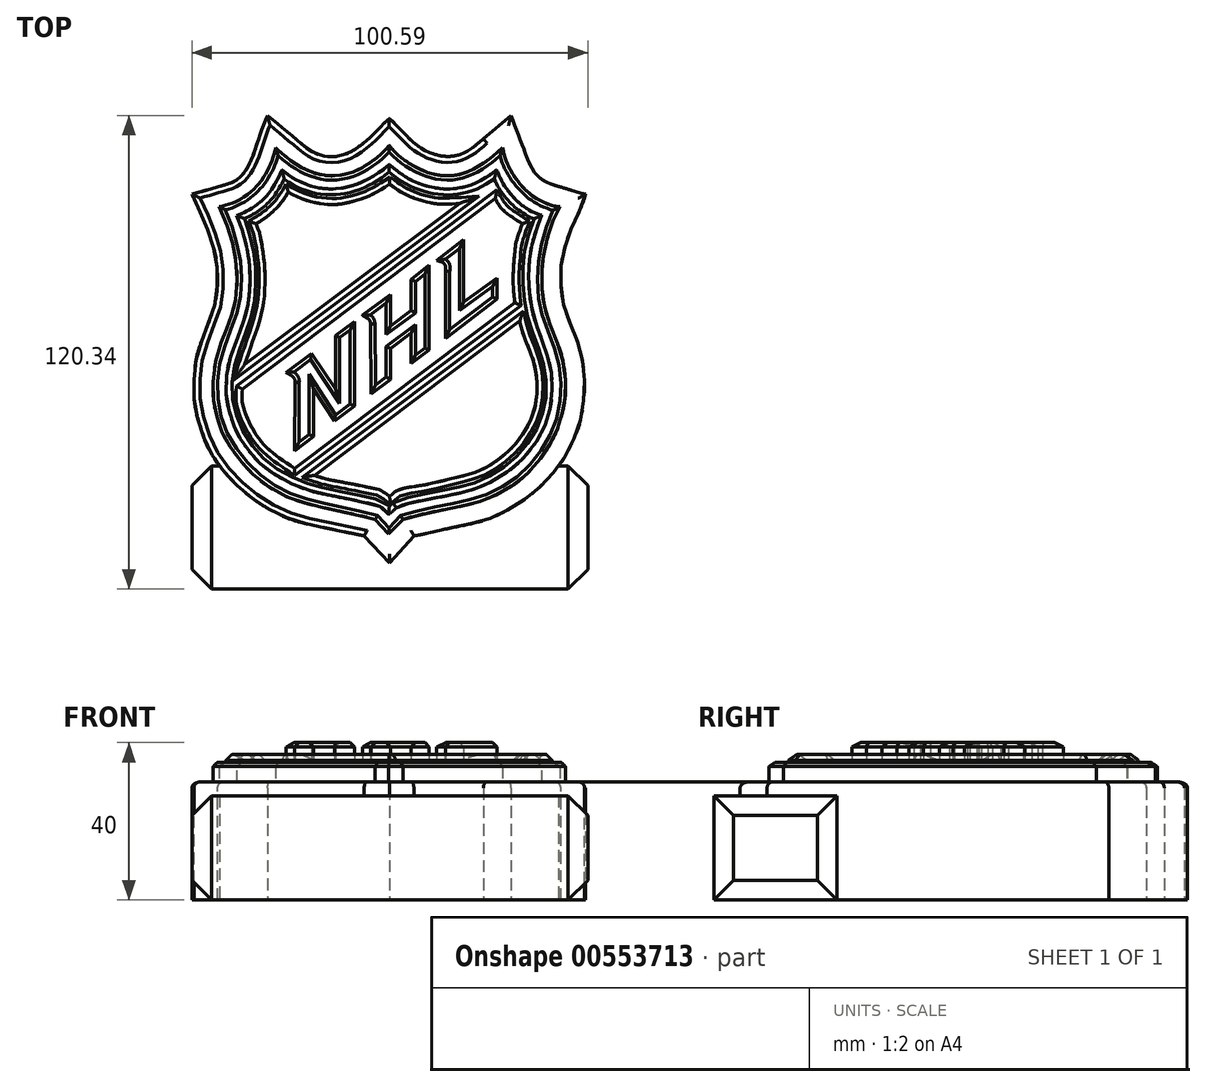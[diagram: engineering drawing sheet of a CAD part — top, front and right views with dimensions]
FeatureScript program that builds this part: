
annotation { "Feature Type Name" : "Feature", "Feature Type Description" : "" }
export const myFeature = defineFeature(function(context is Context, id is Id, definition is map)
    precondition{}
    {
        {
            var Q0;
            Q0=qCreatedBy(makeId("Top.planeOp"),FACE);
            var sketch = newSketch(context, id + "F0", { "sketchPlane" : qUnion([Q0])});
            skLineSegment(sketch, "E0", {"start": v(50, 113.85) * mm, "end": v(50, 0) * mm, "construction": true});
            skLineSegment(sketch, "E1", {"start": v(0, 56.93) * mm, "end": v(100, 56.93) * mm, "construction": true});
            skFitSpline(sketch, "E2", {"points": [v(19.23, 113.85) * mm, v(27.56, 106.9) * mm, v(30.56, 104.67) * mm, v(33.56, 103.56) * mm, v(37.49, 103.58) * mm, v(41.05, 105.05) * mm, v(45.06, 108.09) * mm, v(48.5, 111.55) * mm, v(50.17, 113.1) * mm], "startDerivative": vector(48.33, -40.51) * mm, "endDerivative": vector(17.24, 15.33) * mm});
            skFitSpline(sketch, "E3", {"points": [v(50.17, 113.1) * mm, v(52.88, 110.37) * mm, v(56.85, 106.54) * mm, v(59.8, 104.69) * mm, v(64.07, 103.49) * mm, v(69, 104.28) * mm, v(74.05, 107.95) * mm], "startDerivative": vector(16.76, -16.86) * mm, "endDerivative": vector(25.56, 22.35) * mm});
            skFitSpline(sketch, "E4", {"points": [v(74.05, 107.95) * mm, v(81.12, 113.81) * mm], "startDerivative": vector(7.07, 5.86) * mm, "endDerivative": vector(7.07, 5.86) * mm});
            skFitSpline(sketch, "E5", {"points": [v(81.12, 113.81) * mm, v(81.69, 112.23) * mm, v(82.46, 110.17) * mm, v(83.47, 107.49) * mm, v(84.8, 103.88) * mm, v(85.65, 101.74) * mm, v(87.45, 98.94) * mm, v(89.7, 97.08) * mm, v(92.96, 95.88) * mm, v(97.7, 94.47) * mm, v(100, 93.85) * mm], "startDerivative": vector(7.22, -20.27) * mm, "endDerivative": vector(22.72, -5.9) * mm});
            skFitSpline(sketch, "E6", {"points": [v(100, 93.85) * mm, v(99.63, 92.56) * mm, v(98.68, 90.12) * mm, v(97.69, 87.95) * mm, v(96.72, 85.83) * mm, v(95.29, 82.28) * mm, v(94.02, 77.13) * mm, v(93.73, 74.43) * mm, v(93.84, 69.89) * mm, v(94.57, 65.37) * mm, v(96.14, 60.78) * mm, v(97.7, 56.93) * mm, v(98.46, 54.7) * mm, v(99.33, 50.7) * mm, v(99.66, 47.48) * mm, v(99.7, 44.06) * mm, v(99.26, 39.32) * mm, v(98.41, 35.15) * mm, v(96.8, 31.22) * mm, v(94.63, 26.9) * mm, v(91.9, 23.25) * mm, v(87.6, 18.78) * mm, v(82.5, 15.03) * mm, v(77.28, 12.13) * mm, v(72.01, 10.37) * mm, v(65.55, 9) * mm, v(59.09, 7.54) * mm, v(56.38, 7.05) * mm], "startDerivative": vector(-14.58, -55.75) * mm, "endDerivative": vector(-79.32, -12.44) * mm});
            skFitSpline(sketch, "E7", {"points": [v(56.38, 7.05) * mm, v(50.17, 0.2) * mm], "startDerivative": vector(-6.21, -6.86) * mm, "endDerivative": vector(-6.21, -6.86) * mm});
            skFitSpline(sketch, "E8", {"points": [v(50.17, 0.2) * mm, v(43.77, 7.05) * mm], "startDerivative": vector(-6.4, 6.86) * mm, "endDerivative": vector(-6.4, 6.86) * mm});
            skFitSpline(sketch, "E9", {"points": [v(43.77, 7.05) * mm, v(37.64, 8.3) * mm, v(30.62, 9.78) * mm, v(24.95, 11.31) * mm, v(18.28, 14.6) * mm, v(12.57, 18.84) * mm, v(7.7, 23.96) * mm, v(4.2, 29.3) * mm, v(2.63, 33.24) * mm, v(1, 38.8) * mm, v(0.53, 43.88) * mm, v(0.99, 51.33) * mm, v(2.6, 56.93) * mm, v(4.5, 61.84) * mm, v(5.46, 64.48) * mm, v(6.23, 68.11) * mm, v(6.46, 74.89) * mm, v(5.69, 79.64) * mm, v(4.3, 84.07) * mm, v(2.05, 89.37) * mm, v(0, 93.85) * mm], "startDerivative": vector(-113.2, 22.62) * mm, "endDerivative": vector(-42.94, 93.18) * mm});
            skFitSpline(sketch, "E10", {"points": [v(0, 93.85) * mm, v(7.34, 95.93) * mm, v(11.6, 97.66) * mm, v(14.8, 102.02) * mm, v(17.5, 109.53) * mm, v(19.23, 113.85) * mm], "startDerivative": vector(34.45, 9.76) * mm, "endDerivative": vector(9.58, 22.15) * mm});
            skSolve(sketch);
        }
        {
            var Q0;
            Q0 = qSketchRegion(id + "F0", true);
            extrude(context, id + "F1", {"entities" : qUnion([Q0]), "depth" : 30 * mm, "offsetDistance" : 25 * mm});
        }
        {
            var Q0;
            Q0=makeQuery(id+"F1.opExtrude","CAP_FACE",FACE,{"disambiguationData":[OSD([sQuery(id+"F0.wireOp",EDGE,"E2"),sQuery(id+"F0.wireOp",EDGE,"E3"),sQuery(id+"F0.wireOp",EDGE,"E4"),sQuery(id+"F0.wireOp",EDGE,"E5"),sQuery(id+"F0.wireOp",EDGE,"E6"),sQuery(id+"F0.wireOp",EDGE,"E7"),sQuery(id+"F0.wireOp",EDGE,"E8"),sQuery(id+"F0.wireOp",EDGE,"E9"),sQuery(id+"F0.wireOp",EDGE,"E10")])],"isStart":false});
            var sketch = newSketch(context, id + "F2", { "sketchPlane" : qUnion([Q0])});
            skFitSpline(sketch, "E11", {"points": [v(6.93, 90.68) * mm, v(9.38, 84.53) * mm, v(10.7, 79.56) * mm, v(11.45, 74.35) * mm, v(11.13, 67.25) * mm, v(10.07, 63.23) * mm, v(8.87, 59.83) * mm, v(7.68, 56.76) * mm, v(5.92, 50.72) * mm, v(5.35, 44) * mm, v(5.92, 39.1) * mm, v(7.18, 34.64) * mm, v(8.75, 31.18) * mm, v(12.14, 26.4) * mm, v(15.4, 22.83) * mm, v(20.5, 18.87) * mm, v(26.97, 15.92) * mm, v(31.8, 14.6) * mm, v(38.22, 13.15) * mm, v(44.75, 11.7) * mm, v(46.57, 11.2) * mm], "startDerivative": vector(47.57, -111.38) * mm, "endDerivative": vector(50.2, -15.05) * mm});
            skFitSpline(sketch, "E12", {"points": [v(46.57, 11.2) * mm, v(50, 7.46) * mm], "startDerivative": vector(3.43, -3.75) * mm, "endDerivative": vector(3.43, -3.75) * mm});
            skFitSpline(sketch, "E13", {"points": [v(50, 7.46) * mm, v(53.6, 11.2) * mm], "startDerivative": vector(3.6, 3.75) * mm, "endDerivative": vector(3.6, 3.75) * mm});
            skFitSpline(sketch, "E14", {"points": [v(53.6, 11.2) * mm, v(58.24, 12.46) * mm, v(64.77, 13.84) * mm, v(71.05, 15.2) * mm, v(75.23, 16.58) * mm, v(79.29, 18.56) * mm, v(83.53, 21.35) * mm, v(88.02, 26.03) * mm, v(90.66, 29.77) * mm, v(92.64, 33.67) * mm, v(93.83, 37.18) * mm, v(94.55, 40.51) * mm, v(94.93, 44.7) * mm, v(94.37, 50.79) * mm, v(93.2, 54.97) * mm, v(91.04, 60.56) * mm, v(89.53, 65.5) * mm, v(88.93, 70.58) * mm, v(88.93, 74.95) * mm, v(89.34, 78.28) * mm, v(90.56, 83.59) * mm, v(91.95, 87.54) * mm, v(93.45, 90.65) * mm], "startDerivative": vector(97.04, 28) * mm, "endDerivative": vector(40.44, 78.79) * mm});
            skFitSpline(sketch, "E15", {"points": [v(6.93, 90.68) * mm, v(10.55, 91.69) * mm, v(15.37, 94.79) * mm, v(18.32, 98.34) * mm, v(20.3, 102.26) * mm, v(21.3, 105.7) * mm], "startDerivative": vector(18.82, 3.64) * mm, "endDerivative": vector(4.63, 18.8) * mm});
            skFitSpline(sketch, "E16", {"points": [v(21.3, 105.7) * mm, v(22.88, 104.22) * mm, v(25.74, 101.97) * mm, v(30.3, 99.55) * mm, v(33.76, 98.64) * mm, v(36.89, 98.6) * mm, v(41.37, 99.68) * mm, v(44.15, 101.14) * mm, v(47.55, 103.59) * mm, v(50.13, 106.23) * mm], "startDerivative": vector(17.16, -16.8) * mm, "endDerivative": vector(21.31, 24.02) * mm});
            skFitSpline(sketch, "E17", {"points": [v(50.13, 106.23) * mm, v(51.12, 105.06) * mm, v(52.88, 103.37) * mm, v(55.35, 101.62) * mm, v(57.8, 100.26) * mm, v(61, 99.05) * mm, v(64.11, 98.55) * mm, v(67.14, 98.69) * mm, v(70.55, 99.75) * mm, v(73.46, 101.34) * mm, v(75.97, 103.12) * mm, v(78.88, 105.7) * mm], "startDerivative": vector(14.11, -17.2) * mm, "endDerivative": vector(28.39, 26.46) * mm});
            skFitSpline(sketch, "E18", {"points": [v(78.88, 105.7) * mm, v(79.72, 102.72) * mm, v(81.03, 99.75) * mm, v(83.76, 95.97) * mm, v(87.65, 92.68) * mm, v(91.85, 90.9) * mm, v(93.45, 90.65) * mm], "startDerivative": vector(5, -19.54) * mm, "endDerivative": vector(12.63, -1.1) * mm});
            skSolve(sketch);
        }
        {
            var Q0;
            Q0 = qSketchRegion(id + "F2", true);
            extrude(context, id + "F3", {"entities" : qUnion([Q0]), "operationType" : NewBodyOperationType.ADD, "depth" : 5 * mm, "offsetDistance" : 25 * mm});
        }
        {
            var Q0;
            Q0=makeQuery(id+"F3.opExtrude","CAP_FACE",FACE,{"disambiguationData":[OSD([sQuery(id+"F2.wireOp",EDGE,"E11"),sQuery(id+"F2.wireOp",EDGE,"E12"),sQuery(id+"F2.wireOp",EDGE,"E13"),sQuery(id+"F2.wireOp",EDGE,"E14"),sQuery(id+"F2.wireOp",EDGE,"E15"),sQuery(id+"F2.wireOp",EDGE,"E16"),sQuery(id+"F2.wireOp",EDGE,"E17"),sQuery(id+"F2.wireOp",EDGE,"E18")])],"isStart":false});
            chamfer(context, id + "F4", {"entities" : qUnion([Q0]), "width" : 1.1 * mm, "tangentPropagation" : true});
        }
        {
            var Q0;
            Q0=makeQuery(id+"F1.opExtrude","CAP_EDGE",EDGE,{"disambiguationData":[OSD([sQuery(id+"F0.wireOp",EDGE,"E6")])],"isStart":false});
            var Q1;
            Q1=makeQuery(id+"F1.opExtrude","CAP_EDGE",EDGE,{"disambiguationData":[OSD([sQuery(id+"F0.wireOp",EDGE,"E7")])],"isStart":false});
            var Q2;
            Q2=makeQuery(id+"F1.opExtrude","CAP_EDGE",EDGE,{"disambiguationData":[OSD([sQuery(id+"F0.wireOp",EDGE,"E9")])],"isStart":false});
            var Q3;
            Q3=makeQuery(id+"F1.opExtrude","CAP_EDGE",EDGE,{"disambiguationData":[OSD([sQuery(id+"F0.wireOp",EDGE,"E10")])],"isStart":false});
            var Q4;
            Q4=makeQuery(id+"F1.opExtrude","CAP_EDGE",EDGE,{"disambiguationData":[OSD([sQuery(id+"F0.wireOp",EDGE,"E2")])],"isStart":false});
            var Q5;
            Q5=makeQuery(id+"F1.opExtrude","CAP_EDGE",EDGE,{"disambiguationData":[OSD([sQuery(id+"F0.wireOp",EDGE,"E3")])],"isStart":false});
            var Q6;
            Q6=makeQuery(id+"F1.opExtrude","CAP_EDGE",EDGE,{"disambiguationData":[OSD([sQuery(id+"F0.wireOp",EDGE,"E5")])],"isStart":false});
            var Q7;
            Q7=makeQuery(id+"F1.opExtrude","CAP_EDGE",EDGE,{"disambiguationData":[OSD([sQuery(id+"F0.wireOp",EDGE,"E8")])],"isStart":false});
            var Q8;
            Q8=makeQuery(id+"F1.opExtrude","CAP_EDGE",EDGE,{"disambiguationData":[OSD([sQuery(id+"F0.wireOp",EDGE,"E4")])],"isStart":false});
            fillet(context, id + "F5", {"entities" : qUnion([Q0, Q1, Q2, Q3, Q4, Q5, Q6, Q7, Q8]), "radius" : 1.5 * mm, "tangentPropagation" : true, "allowEdgeOverflow" : false});
        }
        {
            var Q0;
            Q0=makeQuery(id+"F3.opExtrude","CAP_FACE",FACE,{"disambiguationData":[OSD([sQuery(id+"F2.wireOp",EDGE,"E11"),sQuery(id+"F2.wireOp",EDGE,"E12"),sQuery(id+"F2.wireOp",EDGE,"E13"),sQuery(id+"F2.wireOp",EDGE,"E14"),sQuery(id+"F2.wireOp",EDGE,"E15"),sQuery(id+"F2.wireOp",EDGE,"E16"),sQuery(id+"F2.wireOp",EDGE,"E17"),sQuery(id+"F2.wireOp",EDGE,"E18")])],"isStart":false});
            var sketch = newSketch(context, id + "F6", { "sketchPlane" : qUnion([Q0])});
            skFitSpline(sketch, "E19", {"points": [v(11.37, 88.45) * mm, v(12.75, 84.84) * mm, v(14.07, 79.6) * mm, v(14.73, 73.93) * mm, v(14.36, 66.8) * mm, v(13.25, 61.9) * mm, v(11.3, 56.49) * mm, v(9.2, 50.2) * mm, v(8.65, 44.05) * mm, v(9.31, 39.27) * mm, v(10.66, 35.04) * mm, v(12, 32.1) * mm, v(14.54, 28.46) * mm, v(17.27, 25.53) * mm, v(21.73, 22.25) * mm, v(28.36, 19.06) * mm, v(33.06, 17.76) * mm, v(39.61, 16.42) * mm, v(45.66, 15.12) * mm, v(48.33, 14.14) * mm, v(50, 12.48) * mm], "startDerivative": vector(32.13, -77.93) * mm, "endDerivative": vector(45.27, -54.13) * mm});
            skFitSpline(sketch, "E20", {"points": [v(50, 12.48) * mm, v(50.86, 13.19) * mm, v(51.9, 14.14) * mm], "startDerivative": vector(1.78, 1.45) * mm, "endDerivative": vector(2, 1.88) * mm});
            skFitSpline(sketch, "E21", {"points": [v(51.9, 14.14) * mm, v(54.14, 15.04) * mm, v(57.27, 15.8) * mm, v(61.04, 16.52) * mm, v(66.07, 17.5) * mm, v(70.78, 18.64) * mm, v(74.2, 19.92) * mm, v(79.17, 22.64) * mm, v(84, 26.6) * mm, v(88.33, 32.31) * mm, v(90.05, 36.22) * mm, v(91.3, 41) * mm, v(91.48, 46.26) * mm, v(91.02, 50.12) * mm, v(89.72, 54.5) * mm, v(88.39, 58.21) * mm, v(86.99, 62.32) * mm, v(86.04, 66.7) * mm, v(85.64, 70.54) * mm, v(85.59, 74.12) * mm, v(85.93, 78.58) * mm, v(86.63, 82) * mm, v(88, 86.25) * mm, v(88.86, 88.5) * mm], "startDerivative": vector(65.22, 29.34) * mm, "endDerivative": vector(25.15, 61.86) * mm});
            skFitSpline(sketch, "E22", {"points": [v(88.86, 88.5) * mm, v(86.66, 89.3) * mm, v(83.49, 91.33) * mm, v(81.45, 93.3) * mm, v(79.35, 96.03) * mm, v(78.07, 98.49) * mm, v(77.41, 100.02) * mm], "startDerivative": vector(-13.59, 4.04) * mm, "endDerivative": vector(-4.71, 11.2) * mm});
            skFitSpline(sketch, "E23", {"points": [v(77.41, 100.02) * mm, v(75.76, 98.79) * mm, v(72.88, 97.1) * mm, v(69.79, 95.86) * mm, v(66.4, 95.22) * mm, v(63.71, 95.22) * mm, v(60.17, 95.8) * mm, v(56.66, 97) * mm, v(53.74, 98.6) * mm, v(51.2, 100.52) * mm, v(50.15, 101.42) * mm], "startDerivative": vector(-18.12, -14.24) * mm, "endDerivative": vector(-13.41, 11.88) * mm});
            skFitSpline(sketch, "E24", {"points": [v(50.15, 101.42) * mm, v(49.1, 100.53) * mm, v(46.36, 98.57) * mm, v(42.82, 96.77) * mm, v(39.83, 95.75) * mm, v(36.52, 95.21) * mm, v(33.3, 95.32) * mm, v(31.09, 95.67) * mm, v(28.7, 96.5) * mm, v(26.17, 97.7) * mm, v(24.13, 99.03) * mm, v(22.89, 100.02) * mm], "startDerivative": vector(-14.26, -12.25) * mm, "endDerivative": vector(-16.53, 13.74) * mm});
            skFitSpline(sketch, "E25", {"points": [v(22.89, 100.02) * mm, v(22.15, 98.38) * mm, v(20.5, 95.49) * mm, v(19.15, 93.63) * mm, v(16.66, 91.26) * mm, v(13.63, 89.4) * mm, v(11.37, 88.45) * mm], "startDerivative": vector(-4.62, -11.1) * mm, "endDerivative": vector(-13.9, -5.32) * mm});
            skFitSpline(sketch, "E26", {"points": [v(24.48, 94.37) * mm, v(22.17, 91.05) * mm, v(18.5, 87.76) * mm, v(16.26, 86.34) * mm], "startDerivative": vector(-5.87, -9.67) * mm, "endDerivative": vector(-7.52, -4.35) * mm});
            skFitSpline(sketch, "E27", {"points": [v(16.26, 86.34) * mm, v(17.23, 83.65) * mm, v(18.13, 78.35) * mm, v(18.5, 75.02) * mm, v(18.5, 69.45) * mm, v(17.98, 65) * mm, v(16.64, 59.93) * mm, v(14.77, 54.66) * mm, v(13.39, 50.51) * mm], "startDerivative": vector(10.37, -23.68) * mm, "endDerivative": vector(-10.58, -32.85) * mm});
            skLineSegment(sketch, "E28", {"start": v(13.39, 50.51) * mm, "end": v(68.05, 91.51) * mm});
            skFitSpline(sketch, "E29", {"points": [v(24.48, 94.37) * mm, v(28.95, 92.31) * mm, v(33.44, 91.38) * mm, v(37.62, 91.33) * mm, v(42.5, 92.49) * mm, v(45.93, 93.82) * mm, v(50.23, 96.4) * mm], "startDerivative": vector(25.4, -13.36) * mm, "endDerivative": vector(25.52, 16.34) * mm});
            skFitSpline(sketch, "E30", {"points": [v(50.23, 96.4) * mm, v(52.32, 94.93) * mm, v(55.92, 93.07) * mm, v(60.14, 91.78) * mm, v(63.07, 91.33) * mm, v(68.05, 91.51) * mm], "startDerivative": vector(11.74, -8.7) * mm, "endDerivative": vector(23.3, 1.55) * mm});
            skLineSegment(sketch, "E31", {"start": v(12.82, 44.3) * mm, "end": v(77.05, 92.7) * mm});
            skFitSpline(sketch, "E32", {"points": [v(77.05, 92.7) * mm, v(78.84, 90.02) * mm, v(83.95, 86.35) * mm], "startDerivative": vector(3.36, -6.48) * mm, "endDerivative": vector(10.08, -6.24) * mm});
            skFitSpline(sketch, "E33", {"points": [v(83.95, 86.35) * mm, v(82.43, 81.87) * mm, v(82.09, 79.59) * mm, v(81.6, 72.89) * mm, v(82.02, 66.26) * mm], "startDerivative": vector(-7.5, -20.4) * mm, "endDerivative": vector(2.3, -21.83) * mm});
            skLineSegment(sketch, "E34", {"start": v(82.02, 66.26) * mm, "end": v(26.08, 24.2) * mm});
            skFitSpline(sketch, "E35", {"points": [v(12.82, 44.3) * mm, v(12.82, 40.7) * mm, v(15.24, 34.56) * mm, v(18.97, 29.52) * mm, v(26.08, 24.2) * mm], "startDerivative": vector(-1.94, -17.52) * mm, "endDerivative": vector(26.12, -17.5) * mm});
            skLineSegment(sketch, "E36", {"start": v(31.11, 22.4) * mm, "end": v(83.25, 61.56) * mm});
            skFitSpline(sketch, "E37", {"points": [v(83.25, 61.56) * mm, v(84.22, 58.1) * mm, v(86.22, 53.14) * mm, v(87.26, 49.34) * mm, v(87.67, 44.85) * mm, v(86.64, 38.08) * mm, v(82.56, 30.83) * mm, v(79.04, 27.38) * mm, v(73.52, 23.79) * mm, v(67.02, 21.85) * mm, v(60.8, 20.33) * mm, v(56.39, 19.57) * mm, v(52.45, 18.67) * mm, v(50.24, 17.09) * mm], "startDerivative": vector(11.94, -50.95) * mm, "endDerivative": vector(-35.18, -31.83) * mm});
            skFitSpline(sketch, "E38", {"points": [v(50.24, 17.09) * mm, v(49.45, 17.64) * mm, v(48.07, 18.54) * mm, v(45.86, 19.16) * mm, v(40.26, 20.3) * mm, v(33.94, 21.54) * mm, v(31.11, 22.4) * mm], "startDerivative": vector(-7.9, 5.34) * mm, "endDerivative": vector(-15.3, 5.29) * mm});
            skSolve(sketch);
        }
        {
            var Q0;
            Q0 = qSketchRegion(id + "F6", true);
            extrude(context, id + "F7", {"entities" : qUnion([Q0]), "operationType" : NewBodyOperationType.ADD, "depth" : 2 * mm, "offsetDistance" : 25 * mm});
        }
        {
            var Q0;
            Q0=qCreatedBy(makeId("Top.planeOp"),FACE);
            var sketch = newSketch(context, id + "F8", { "sketchPlane" : qUnion([Q0])});
            skLineSegment(sketch, "E39", {"start": v(26.13, 28.62) * mm, "end": v(30.9, 32.23) * mm});
            skLineSegment(sketch, "E40", {"start": v(30.9, 32.23) * mm, "end": v(30.9, 44.39) * mm});
            skLineSegment(sketch, "E41", {"start": v(30.9, 44.39) * mm, "end": v(36.22, 36.19) * mm});
            skLineSegment(sketch, "E42", {"start": v(36.22, 36.19) * mm, "end": v(41.26, 40.02) * mm});
            skLineSegment(sketch, "E43", {"start": v(41.26, 40.02) * mm, "end": v(41.26, 61.46) * mm});
            skLineSegment(sketch, "E44", {"start": v(41.26, 61.46) * mm, "end": v(36.44, 57.95) * mm});
            skLineSegment(sketch, "E45", {"start": v(36.44, 57.95) * mm, "end": v(36.44, 44.3) * mm});
            skLineSegment(sketch, "E46", {"start": v(36.44, 44.3) * mm, "end": v(30.36, 53.4) * mm});
            skLineSegment(sketch, "E47", {"start": v(30.36, 53.4) * mm, "end": v(23.97, 48.53) * mm});
            skFitSpline(sketch, "E48", {"points": [v(23.97, 48.53) * mm, v(24.91, 48) * mm, v(26.04, 46.96) * mm, v(26.17, 45.96) * mm], "startDerivative": vector(2.8, -1.47) * mm, "endDerivative": vector(-0.17, -3.3) * mm});
            skLineSegment(sketch, "E49", {"start": v(26.13, 28.62) * mm, "end": v(26.17, 45.96) * mm});
            skLineSegment(sketch, "E50", {"start": v(45.51, 43.13) * mm, "end": v(50.42, 46.78) * mm});
            skLineSegment(sketch, "E51", {"start": v(50.42, 46.78) * mm, "end": v(50.42, 54.62) * mm});
            skLineSegment(sketch, "E52", {"start": v(50.42, 54.62) * mm, "end": v(55.65, 58.54) * mm});
            skLineSegment(sketch, "E53", {"start": v(55.65, 58.54) * mm, "end": v(55.65, 50.84) * mm});
            skLineSegment(sketch, "E54", {"start": v(55.65, 50.84) * mm, "end": v(60.29, 54.21) * mm});
            skLineSegment(sketch, "E55", {"start": v(60.29, 54.21) * mm, "end": v(60.29, 75.84) * mm});
            skLineSegment(sketch, "E56", {"start": v(60.29, 75.84) * mm, "end": v(55.65, 72.14) * mm});
            skLineSegment(sketch, "E57", {"start": v(55.65, 72.14) * mm, "end": v(55.65, 64.26) * mm});
            skLineSegment(sketch, "E58", {"start": v(55.65, 64.26) * mm, "end": v(50.42, 60.39) * mm});
            skLineSegment(sketch, "E59", {"start": v(50.42, 60.39) * mm, "end": v(50.42, 68.36) * mm});
            skLineSegment(sketch, "E60", {"start": v(50.42, 68.36) * mm, "end": v(43.33, 63.1) * mm});
            skFitSpline(sketch, "E61", {"points": [v(43.33, 63.1) * mm, v(44.12, 62.6) * mm, v(45.02, 62) * mm, v(45.42, 60.84) * mm], "startDerivative": vector(2.4, -1.7) * mm, "endDerivative": vector(0.69, -3.69) * mm});
            skLineSegment(sketch, "E62", {"start": v(45.42, 60.84) * mm, "end": v(45.51, 43.13) * mm});
            skLineSegment(sketch, "E63", {"start": v(77.46, 72.58) * mm, "end": v(77.46, 67.17) * mm});
            skLineSegment(sketch, "E64", {"start": v(77.46, 67.17) * mm, "end": v(64.39, 57.2) * mm});
            skLineSegment(sketch, "E65", {"start": v(64.39, 57.2) * mm, "end": v(64.39, 74.3) * mm});
            skLineSegment(sketch, "E66", {"start": v(62.2, 76.98) * mm, "end": v(69.05, 82.28) * mm});
            skLineSegment(sketch, "E67", {"start": v(69.05, 82.28) * mm, "end": v(69.05, 66.48) * mm});
            skLineSegment(sketch, "E68", {"start": v(69.05, 66.48) * mm, "end": v(77.46, 72.58) * mm});
            skFitSpline(sketch, "E69", {"points": [v(62.2, 76.98) * mm, v(63.58, 76.55) * mm, v(64.39, 75.7) * mm, v(64.39, 74.3) * mm], "startDerivative": vector(4.23, -0.9) * mm, "endDerivative": vector(-0.62, -4.37) * mm});
            skSolve(sketch);
        }
        {
            var Q0;
            Q0 = qSketchRegion(id + "F8", true);
            extrude(context, id + "F9", {"entities" : qUnion([Q0]), "operationType" : NewBodyOperationType.ADD, "depth" : 40 * mm, "offsetDistance" : 25 * mm});
        }
        {
            var Q0;
            Q0=makeQuery(id+"F9.opExtrude","CAP_FACE",FACE,{"disambiguationData":[OSD([sQuery(id+"F8.wireOp",EDGE,"E39"),sQuery(id+"F8.wireOp",EDGE,"E40"),sQuery(id+"F8.wireOp",EDGE,"E41"),sQuery(id+"F8.wireOp",EDGE,"E42"),sQuery(id+"F8.wireOp",EDGE,"E43"),sQuery(id+"F8.wireOp",EDGE,"E44"),sQuery(id+"F8.wireOp",EDGE,"E45"),sQuery(id+"F8.wireOp",EDGE,"E46"),sQuery(id+"F8.wireOp",EDGE,"E47"),sQuery(id+"F8.wireOp",EDGE,"E48"),sQuery(id+"F8.wireOp",EDGE,"E49")])],"isStart":false});
            var Q1;
            Q1=makeQuery(id+"F9.opExtrude","CAP_FACE",FACE,{"disambiguationData":[OSD([sQuery(id+"F8.wireOp",EDGE,"E50"),sQuery(id+"F8.wireOp",EDGE,"E51"),sQuery(id+"F8.wireOp",EDGE,"E52"),sQuery(id+"F8.wireOp",EDGE,"E53"),sQuery(id+"F8.wireOp",EDGE,"E54"),sQuery(id+"F8.wireOp",EDGE,"E55"),sQuery(id+"F8.wireOp",EDGE,"E56"),sQuery(id+"F8.wireOp",EDGE,"E57"),sQuery(id+"F8.wireOp",EDGE,"E58"),sQuery(id+"F8.wireOp",EDGE,"E59"),sQuery(id+"F8.wireOp",EDGE,"E60"),sQuery(id+"F8.wireOp",EDGE,"E61"),sQuery(id+"F8.wireOp",EDGE,"E62")])],"isStart":false});
            var Q2;
            Q2=makeQuery(id+"F9.opExtrude","CAP_FACE",FACE,{"disambiguationData":[OSD([sQuery(id+"F8.wireOp",EDGE,"E63"),sQuery(id+"F8.wireOp",EDGE,"E64"),sQuery(id+"F8.wireOp",EDGE,"E65"),sQuery(id+"F8.wireOp",EDGE,"E66"),sQuery(id+"F8.wireOp",EDGE,"E67"),sQuery(id+"F8.wireOp",EDGE,"E68"),sQuery(id+"F8.wireOp",EDGE,"E69")])],"isStart":false});
            chamfer(context, id + "F10", {"entities" : qUnion([Q0, Q1, Q2]), "width" : 1.1 * mm, "tangentPropagation" : true});
        }
        {
            var Q0;
            Q0=makeQuery(id+"F7.opExtrude","CAP_FACE",FACE,{"disambiguationData":[OSD([sQuery(id+"F6.wireOp",EDGE,"E19"),sQuery(id+"F6.wireOp",EDGE,"E20"),sQuery(id+"F6.wireOp",EDGE,"E21"),sQuery(id+"F6.wireOp",EDGE,"E22"),sQuery(id+"F6.wireOp",EDGE,"E23"),sQuery(id+"F6.wireOp",EDGE,"E24"),sQuery(id+"F6.wireOp",EDGE,"E25"),sQuery(id+"F6.wireOp",EDGE,"E26"),sQuery(id+"F6.wireOp",EDGE,"E27"),sQuery(id+"F6.wireOp",EDGE,"E28"),sQuery(id+"F6.wireOp",EDGE,"E29"),sQuery(id+"F6.wireOp",EDGE,"E30"),sQuery(id+"F6.wireOp",EDGE,"E31"),sQuery(id+"F6.wireOp",EDGE,"E32"),sQuery(id+"F6.wireOp",EDGE,"E33"),sQuery(id+"F6.wireOp",EDGE,"E34"),sQuery(id+"F6.wireOp",EDGE,"E35"),sQuery(id+"F6.wireOp",EDGE,"E36"),sQuery(id+"F6.wireOp",EDGE,"E37"),sQuery(id+"F6.wireOp",EDGE,"E38")])],"isStart":false});
            chamfer(context, id + "F11", {"entities" : qUnion([Q0]), "width" : 1.5 * mm, "tangentPropagation" : true});
        }
        {
            var Q0;
            Q0=qCreatedBy(makeId("Top.planeOp"),FACE);
            var sketch = newSketch(context, id + "F12", { "sketchPlane" : qUnion([Q0])});
            skLineSegment(sketch, "E70", {"start": v(50.3, 0) * mm, "end": v(50.3, -16.78) * mm});
            skLineSegment(sketch, "E71", {"start": v(50.3, -6.5) * mm, "end": v(0, -6.5) * mm});
            skLineSegment(sketch, "E72", {"start": v(0, -6.5) * mm, "end": v(0, 24.78) * mm});
            skLineSegment(sketch, "E73", {"start": v(0, 24.78) * mm, "end": v(50.9, 24.78) * mm});
            skLineSegment(sketch, "E74.MirrorCS", {"start": v(50.3, -6.5) * mm, "end": v(100.6, -6.5) * mm});
            skLineSegment(sketch, "E75.MirrorCS", {"start": v(100.6, -6.5) * mm, "end": v(100.6, 24.78) * mm});
            skLineSegment(sketch, "E76.MirrorCS", {"start": v(100.6, 24.78) * mm, "end": v(49.7, 24.78) * mm});
            skSolve(sketch);
        }
        {
            var Q0;
            Q0 = qSketchRegion(id + "F12", true);
            extrude(context, id + "F13", {"entities" : qUnion([Q0]), "operationType" : NewBodyOperationType.ADD, "depth" : 26.5 * mm, "offsetDistance" : 25 * mm});
        }
        {
            var Q0;
            Q0=makeQuery(id+"F13.opExtrude","SWEPT_FACE",FACE,{"disambiguationData":[OSD([sQuery(id+"F12.wireOp",EDGE,"E72")])]});
            chamfer(context, id + "F14", {"entities" : qUnion([Q0]), "width" : 5 * mm, "tangentPropagation" : true});
        }
        {
            var Q0;
            Q0=makeQuery(id+"F13.opExtrude","SWEPT_FACE",FACE,{"disambiguationData":[OSD([sQuery(id+"F12.wireOp",EDGE,"E75.MirrorCS")])]});
            chamfer(context, id + "F15", {"entities" : qUnion([Q0]), "width" : 5 * mm, "tangentPropagation" : true});
        }
    });
